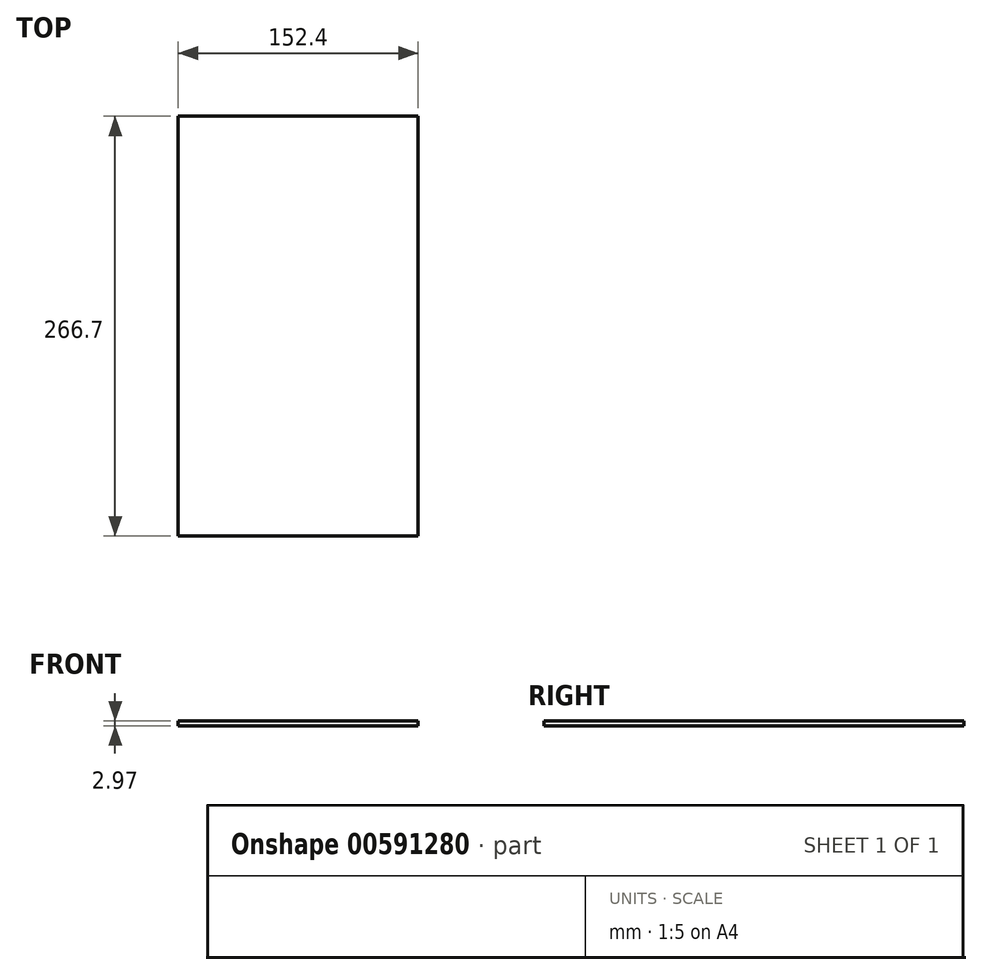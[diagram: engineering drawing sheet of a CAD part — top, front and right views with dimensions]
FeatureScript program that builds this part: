
annotation { "Feature Type Name" : "Feature", "Feature Type Description" : "" }
export const myFeature = defineFeature(function(context is Context, id is Id, definition is map)
    precondition{}
    {
        {
            var Q0;
            Q0=qCreatedBy(makeId("Top.planeOp"),FACE);
            var sketch = newSketch(context, id + "F0", { "sketchPlane" : qUnion([Q0])});
            skLineSegment(sketch, "E0.bottom", {"start": v(76.2, -133.35) * mm, "end": v(-76.2, -133.35) * mm});
            skLineSegment(sketch, "E0.top", {"start": v(76.2, 133.35) * mm, "end": v(-76.2, 133.35) * mm});
            skLineSegment(sketch, "E0.left", {"start": v(76.2, -133.35) * mm, "end": v(76.2, 133.35) * mm});
            skLineSegment(sketch, "E0.right", {"start": v(-76.2, -133.35) * mm, "end": v(-76.2, 133.35) * mm});
            skPoint(sketch, "E0.middle", {"position": v(0, 0) * mm});
            skSolve(sketch);
        }
        {
            var Q0;
            Q0=makeQuery(id+"F0.imprint","IMPRINT",FACE,{"disambiguationData":[TD([[makeQuery(id+"F0.imprint","IMPRINT",EDGE,{"derivedFrom":sQuery(id+"F0.wireOp",EDGE,"E0.bottom")}),-1.0]])]});
            extrude(context, id + "F1", {"entities" : qUnion([Q0]), "depth" : 2.97 * mm, "offsetDistance" : 25.4 * mm});
        }
    });
